# Revit family: Sanitary_Mirrors_Sloan-Valve_MF-Wide-Framea
name_source: partatom
category: Furniture
units: mm (PartAtom-declared; Revit-internal decimal feet)

## family parameters
Cut with Voids When Loaded = No
Host = Face
OmniClass Number = 23.40.95.17.17
OmniClass Title = Mirrors
Room Calculation Point = No
Shared = No

## types (6) — shared parameters
Custom Size Note = Please reach out to Sloan Valve Company for information on custom sizes.
Default Elevation = 48 "
Depth = 0.83 "
Height = 36 "
Manufacturer = Sloan Valve
Product data url = https://bimobject.com
Real Height = 36 "
URL = www.sloanvalve.com
Version = 1
z_Case Back Height = 35.55 "
z_Cutout Height = 2.56 "
z_Cutout Width = 1.5 "
z_Wall Panel Left Offset = 1.72 "
z_Wall Panel Top Offset = 0.87 "
z_Wall Panel Width 1 = 1.97 "
z_Wall Panel Width 2 = 1.5 "

## per-type parameters (varying)
| type | Description | Part Number | Product Material | Real Width | Weight | Width | z_Case Back Width |
| MF Wide Frame-18x36-BN | 18" x 36", Brushed Nickel, Sloan 2" Wall-hung Wide Frame Mirror. | 32910023 | Sloan Valve - Finish - Brushed Nickel | 18 " | 28.00 lbf | 18 " | 17.55 " |
| MF Wide Frame-24x36-CP | 24" x 36", Polished Chrome, Sloan 2" Wall-hung Wide Frame Mirror. | 32910010 | Sloan Valve - Finish - Polished Chrome | 24 " | 36.00 lbf | 24 " | 23.55 " |
| MF Wide Frame-24x36-GR | 24" x 36", Graphite, Sloan 2" Wall-hung Wide Frame Mirror. | 32910006 | Sloan Valve - Finish - Graphite | 24 " | 36.00 lbf | 24 " | 23.55 " |
| MF Wide Frame-18x36-GR | 18" x 36", Graphite, Sloan 2" Wall-hung Wide Frame Mirror. | 32910021 | Sloan Valve - Finish - Graphite | 18 " | 28.00 lbf | 18 " | 17.55 " |
| MF Wide Frame-24x36-BN | 24" x 36", Brushed Nickel, Sloan 2" Wall-hung Wide Frame Mirror. | 32910008 | Sloan Valve - Finish - Brushed Nickel | 24 " | 36.00 lbf | 24 " | 23.55 " |
| MF Wide Frame-18x36-CP | 18" x 36", Polished Chrome, Sloan 2" Wall-hung Wide Frame Mirror. | 32910025 | Sloan Valve - Finish - Polished Chrome | 18 " | 28.00 lbf | 18 " | 17.55 " |

note: column(s) folded — value = type name in every type: Model

## geometry (parser evidence)
native form markers: Sweep x2
no freeform markers — native parametric forms only
